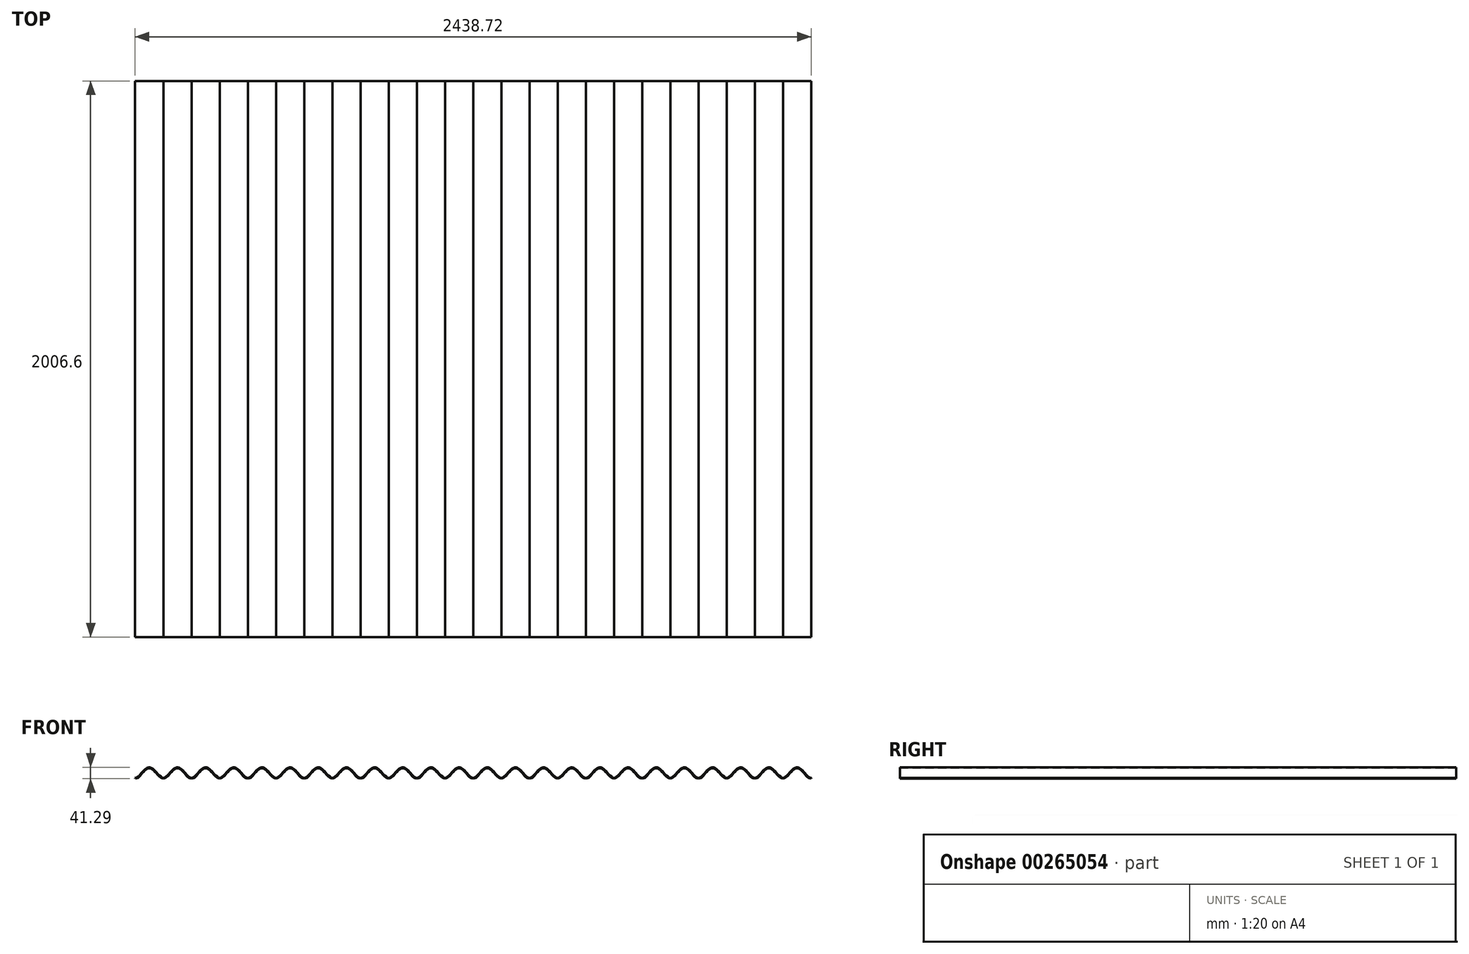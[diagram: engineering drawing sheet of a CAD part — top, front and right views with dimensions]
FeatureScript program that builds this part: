
annotation { "Feature Type Name" : "Feature", "Feature Type Description" : "" }
export const myFeature = defineFeature(function(context is Context, id is Id, definition is map)
    precondition{}
    {
        {
            var Q0;
            Q0=qCreatedBy(makeId("Front.planeOp"),FACE);
            var sketch = newSketch(context, id + "F0", { "sketchPlane" : qUnion([Q0])});
            skFitSpline(sketch, "E0", {"points": [v(-101.6, 0) * mm, v(-76.2, 19.05) * mm, v(-50.8, 38.1) * mm, v(-25.4, 19.05) * mm, v(0, 0) * mm], "startDerivative": vector(131.34, 13.35) * mm, "endDerivative": vector(107.4, -17.1) * mm});
            skLineSegment(sketch, "E1", {"start": v(-101.6, 0) * mm, "end": v(0, 0) * mm, "construction": true});
            skLineSegment(sketch, "E2", {"start": v(-50.8, 49.06) * mm, "end": v(-50.8, -10.5) * mm, "construction": true});
            skPoint(sketch, "E2.endSnap0", {"position": v(-50.8, 0) * mm});
            skFitSpline(sketch, "E3.MirrorCS", {"points": [v(101.6, 0) * mm, v(76.2, 19.05) * mm, v(50.8, 38.1) * mm, v(25.4, 19.05) * mm, v(0, 0) * mm], "startDerivative": vector(-131.34, 13.35) * mm, "endDerivative": vector(-107.4, -17.1) * mm});
            skFitSpline(sketch, "E4.MirrorCS", {"points": [v(101.6, 0) * mm, v(127, 19.05) * mm, v(152.4, 38.1) * mm, v(177.8, 19.05) * mm, v(203.2, 0) * mm], "startDerivative": vector(131.34, 13.35) * mm, "endDerivative": vector(107.4, -17.1) * mm});
            skFitSpline(sketch, "E5.MirrorCS", {"points": [v(304.8, 0) * mm, v(279.4, 19.05) * mm, v(254, 38.1) * mm, v(228.6, 19.05) * mm, v(203.2, 0) * mm], "startDerivative": vector(-131.34, 13.35) * mm, "endDerivative": vector(-107.4, -17.1) * mm});
            skFitSpline(sketch, "E6.MirrorCS", {"points": [v(304.8, 0) * mm, v(330.2, 19.05) * mm, v(355.6, 38.1) * mm, v(381, 19.05) * mm, v(406.4, 0) * mm], "startDerivative": vector(131.34, 13.35) * mm, "endDerivative": vector(107.4, -17.1) * mm});
            skFitSpline(sketch, "E7.MirrorCS", {"points": [v(508, 0) * mm, v(482.6, 19.05) * mm, v(457.2, 38.1) * mm, v(431.8, 19.05) * mm, v(406.4, 0) * mm], "startDerivative": vector(-131.34, 13.35) * mm, "endDerivative": vector(-107.4, -17.1) * mm});
            skFitSpline(sketch, "E8.MirrorCS", {"points": [v(508, 0) * mm, v(533.4, 19.05) * mm, v(558.8, 38.1) * mm, v(584.2, 19.05) * mm, v(609.6, 0) * mm], "startDerivative": vector(131.34, 13.35) * mm, "endDerivative": vector(107.4, -17.1) * mm});
            skFitSpline(sketch, "E9.MirrorCS", {"points": [v(711.2, 0) * mm, v(685.8, 19.05) * mm, v(660.4, 38.1) * mm, v(635, 19.05) * mm, v(609.6, 0) * mm], "startDerivative": vector(-131.34, 13.35) * mm, "endDerivative": vector(-107.4, -17.1) * mm});
            skFitSpline(sketch, "E10.MirrorCS", {"points": [v(711.2, 0) * mm, v(736.6, 19.05) * mm, v(762, 38.1) * mm, v(787.4, 19.05) * mm, v(812.8, 0) * mm], "startDerivative": vector(131.34, 13.35) * mm, "endDerivative": vector(107.4, -17.1) * mm});
            skFitSpline(sketch, "E11.MirrorCS", {"points": [v(914.4, 0) * mm, v(889, 19.05) * mm, v(863.6, 38.1) * mm, v(838.2, 19.05) * mm, v(812.8, 0) * mm], "startDerivative": vector(-131.34, 13.35) * mm, "endDerivative": vector(-107.4, -17.1) * mm});
            skFitSpline(sketch, "E12.MirrorCS", {"points": [v(914.4, 0) * mm, v(939.8, 19.05) * mm, v(965.2, 38.1) * mm, v(990.6, 19.05) * mm, v(1016, 0) * mm], "startDerivative": vector(131.34, 13.35) * mm, "endDerivative": vector(107.4, -17.1) * mm});
            skFitSpline(sketch, "E13.MirrorCS", {"points": [v(1117.6, 0) * mm, v(1092.2, 19.05) * mm, v(1066.8, 38.1) * mm, v(1041.4, 19.05) * mm, v(1016, 0) * mm], "startDerivative": vector(-131.34, 13.35) * mm, "endDerivative": vector(-107.4, -17.1) * mm});
            skFitSpline(sketch, "E14.MirrorCS", {"points": [v(1117.6, 0) * mm, v(1143, 19.05) * mm, v(1168.4, 38.1) * mm, v(1193.8, 19.05) * mm, v(1219.2, 0) * mm], "startDerivative": vector(131.34, 13.35) * mm, "endDerivative": vector(107.4, -17.1) * mm});
            skFitSpline(sketch, "E15.MirrorCS", {"points": [v(1320.8, 0) * mm, v(1295.4, 19.05) * mm, v(1270, 38.1) * mm, v(1244.6, 19.05) * mm, v(1219.2, 0) * mm], "startDerivative": vector(-131.34, 13.35) * mm, "endDerivative": vector(-107.4, -17.1) * mm});
            skFitSpline(sketch, "E16.MirrorCS", {"points": [v(1320.8, 0) * mm, v(1346.2, 19.05) * mm, v(1371.6, 38.1) * mm, v(1397, 19.05) * mm, v(1422.4, 0) * mm], "startDerivative": vector(131.34, 13.35) * mm, "endDerivative": vector(107.4, -17.1) * mm});
            skFitSpline(sketch, "E17.MirrorCS", {"points": [v(1524, 0) * mm, v(1498.6, 19.05) * mm, v(1473.2, 38.1) * mm, v(1447.8, 19.05) * mm, v(1422.4, 0) * mm], "startDerivative": vector(-131.34, 13.35) * mm, "endDerivative": vector(-107.4, -17.1) * mm});
            skFitSpline(sketch, "E18.MirrorCS", {"points": [v(1524, 0) * mm, v(1549.4, 19.05) * mm, v(1574.8, 38.1) * mm, v(1600.2, 19.05) * mm, v(1625.6, 0) * mm], "startDerivative": vector(131.34, 13.35) * mm, "endDerivative": vector(107.4, -17.1) * mm});
            skFitSpline(sketch, "E19.MirrorCS", {"points": [v(1727.2, 0) * mm, v(1701.8, 19.05) * mm, v(1676.4, 38.1) * mm, v(1651, 19.05) * mm, v(1625.6, 0) * mm], "startDerivative": vector(-131.34, 13.35) * mm, "endDerivative": vector(-107.4, -17.1) * mm});
            skFitSpline(sketch, "E20.MirrorCS", {"points": [v(1727.2, 0) * mm, v(1752.6, 19.05) * mm, v(1778, 38.1) * mm, v(1803.4, 19.05) * mm, v(1828.8, 0) * mm], "startDerivative": vector(131.34, 13.35) * mm, "endDerivative": vector(107.4, -17.1) * mm});
            skFitSpline(sketch, "E21.MirrorCS", {"points": [v(1930.4, 0) * mm, v(1905, 19.05) * mm, v(1879.6, 38.1) * mm, v(1854.2, 19.05) * mm, v(1828.8, 0) * mm], "startDerivative": vector(-131.34, 13.35) * mm, "endDerivative": vector(-107.4, -17.1) * mm});
            skFitSpline(sketch, "E22.MirrorCS", {"points": [v(1930.4, 0) * mm, v(1955.8, 19.05) * mm, v(1981.2, 38.1) * mm, v(2006.6, 19.05) * mm, v(2032, 0) * mm], "startDerivative": vector(131.34, 13.35) * mm, "endDerivative": vector(107.4, -17.1) * mm});
            skFitSpline(sketch, "E23.MirrorCS", {"points": [v(2133.6, 0) * mm, v(2108.2, 19.05) * mm, v(2082.8, 38.1) * mm, v(2057.4, 19.05) * mm, v(2032, 0) * mm], "startDerivative": vector(-131.34, 13.35) * mm, "endDerivative": vector(-107.4, -17.1) * mm});
            skFitSpline(sketch, "E24.MirrorCS", {"points": [v(2133.6, 0) * mm, v(2159, 19.05) * mm, v(2184.4, 38.1) * mm, v(2209.8, 19.05) * mm, v(2235.2, 0) * mm], "startDerivative": vector(131.34, 13.35) * mm, "endDerivative": vector(107.4, -17.1) * mm});
            skFitSpline(sketch, "E25.MirrorCS", {"points": [v(2336.8, 0) * mm, v(2311.4, 19.05) * mm, v(2286, 38.1) * mm, v(2260.6, 19.05) * mm, v(2235.2, 0) * mm], "startDerivative": vector(-131.34, 13.35) * mm, "endDerivative": vector(-107.4, -17.1) * mm});
            skFitSpline(sketch, "E26.MirrorCS", {"points": [v(3149.6, 0) * mm, v(3124.2, 19.05) * mm, v(3098.8, 38.1) * mm, v(3073.4, 19.05) * mm, v(3048, 0) * mm], "startDerivative": vector(-131.34, 13.35) * mm, "endDerivative": vector(-107.4, -17.1) * mm});
            skFitSpline(sketch, "E27.MirrorCS", {"points": [v(1930.4, 0) * mm, v(1905, 19.05) * mm, v(1879.6, 38.1) * mm, v(1854.2, 19.05) * mm, v(1828.8, 0) * mm], "startDerivative": vector(-131.34, 13.35) * mm, "endDerivative": vector(-107.4, -17.1) * mm});
            skFitSpline(sketch, "E28.MirrorCS", {"points": [v(1320.8, 0) * mm, v(1295.4, 19.05) * mm, v(1270, 38.1) * mm, v(1244.6, 19.05) * mm, v(1219.2, 0) * mm], "startDerivative": vector(-131.34, 13.35) * mm, "endDerivative": vector(-107.4, -17.1) * mm});
            skFitSpline(sketch, "E29.MirrorCS", {"points": [v(1117.6, 0) * mm, v(1143, 19.05) * mm, v(1168.4, 38.1) * mm, v(1193.8, 19.05) * mm, v(1219.2, 0) * mm], "startDerivative": vector(131.34, 13.35) * mm, "endDerivative": vector(107.4, -17.1) * mm});
            skFitSpline(sketch, "E30.MirrorCS", {"points": [v(1727.2, 0) * mm, v(1752.6, 19.05) * mm, v(1778, 38.1) * mm, v(1803.4, 19.05) * mm, v(1828.8, 0) * mm], "startDerivative": vector(131.34, 13.35) * mm, "endDerivative": vector(107.4, -17.1) * mm});
            skFitSpline(sketch, "E31.MirrorCS", {"points": [v(1930.4, 0) * mm, v(1955.8, 19.05) * mm, v(1981.2, 38.1) * mm, v(2006.6, 19.05) * mm, v(2032, 0) * mm], "startDerivative": vector(131.34, 13.35) * mm, "endDerivative": vector(107.4, -17.1) * mm});
            skFitSpline(sketch, "E32.MirrorCS", {"points": [v(1320.8, 0) * mm, v(1346.2, 19.05) * mm, v(1371.6, 38.1) * mm, v(1397, 19.05) * mm, v(1422.4, 0) * mm], "startDerivative": vector(131.34, 13.35) * mm, "endDerivative": vector(107.4, -17.1) * mm});
            skFitSpline(sketch, "E33.MirrorCS", {"points": [v(1524, 0) * mm, v(1498.6, 19.05) * mm, v(1473.2, 38.1) * mm, v(1447.8, 19.05) * mm, v(1422.4, 0) * mm], "startDerivative": vector(-131.34, 13.35) * mm, "endDerivative": vector(-107.4, -17.1) * mm});
            skFitSpline(sketch, "E34.MirrorCS", {"points": [v(2336.8, 0) * mm, v(2311.4, 19.05) * mm, v(2286, 38.1) * mm, v(2260.6, 19.05) * mm, v(2235.2, 0) * mm], "startDerivative": vector(-131.34, 13.35) * mm, "endDerivative": vector(-107.4, -17.1) * mm});
            skFitSpline(sketch, "E35.MirrorCS", {"points": [v(2336.8, 0) * mm, v(2362.2, 19.05) * mm, v(2387.6, 38.1) * mm, v(2413, 19.05) * mm, v(2438.4, 0) * mm], "startDerivative": vector(131.34, 13.35) * mm, "endDerivative": vector(107.4, -17.1) * mm});
            skFitSpline(sketch, "E36.MirrorCS", {"points": [v(2540, 0) * mm, v(2514.6, 19.05) * mm, v(2489.2, 38.1) * mm, v(2463.8, 19.05) * mm, v(2438.4, 0) * mm], "startDerivative": vector(-131.34, 13.35) * mm, "endDerivative": vector(-107.4, -17.1) * mm});
            skFitSpline(sketch, "E37.MirrorCS", {"points": [v(2540, 0) * mm, v(2565.4, 19.05) * mm, v(2590.8, 38.1) * mm, v(2616.2, 19.05) * mm, v(2641.6, 0) * mm], "startDerivative": vector(131.34, 13.35) * mm, "endDerivative": vector(107.4, -17.1) * mm});
            skFitSpline(sketch, "E38.MirrorCS", {"points": [v(2743.2, 0) * mm, v(2717.8, 19.05) * mm, v(2692.4, 38.1) * mm, v(2667, 19.05) * mm, v(2641.6, 0) * mm], "startDerivative": vector(-131.34, 13.35) * mm, "endDerivative": vector(-107.4, -17.1) * mm});
            skFitSpline(sketch, "E39.MirrorCS", {"points": [v(2133.6, 0) * mm, v(2159, 19.05) * mm, v(2184.4, 38.1) * mm, v(2209.8, 19.05) * mm, v(2235.2, 0) * mm], "startDerivative": vector(131.34, 13.35) * mm, "endDerivative": vector(107.4, -17.1) * mm});
            skFitSpline(sketch, "E40.MirrorCS", {"points": [v(1727.2, 0) * mm, v(1701.8, 19.05) * mm, v(1676.4, 38.1) * mm, v(1651, 19.05) * mm, v(1625.6, 0) * mm], "startDerivative": vector(-131.34, 13.35) * mm, "endDerivative": vector(-107.4, -17.1) * mm});
            skFitSpline(sketch, "E41.MirrorCS", {"points": [v(2743.2, 0) * mm, v(2768.6, 19.05) * mm, v(2794, 38.1) * mm, v(2819.4, 19.05) * mm, v(2844.8, 0) * mm], "startDerivative": vector(131.34, 13.35) * mm, "endDerivative": vector(107.4, -17.1) * mm});
            skFitSpline(sketch, "E42.MirrorCS", {"points": [v(1524, 0) * mm, v(1549.4, 19.05) * mm, v(1574.8, 38.1) * mm, v(1600.2, 19.05) * mm, v(1625.6, 0) * mm], "startDerivative": vector(131.34, 13.35) * mm, "endDerivative": vector(107.4, -17.1) * mm});
            skFitSpline(sketch, "E43.MirrorCS", {"points": [v(914.4, 0) * mm, v(939.8, 19.05) * mm, v(965.2, 38.1) * mm, v(990.6, 19.05) * mm, v(1016, 0) * mm], "startDerivative": vector(131.34, 13.35) * mm, "endDerivative": vector(107.4, -17.1) * mm});
            skFitSpline(sketch, "E44.MirrorCS", {"points": [v(2946.4, 0) * mm, v(2921, 19.05) * mm, v(2895.6, 38.1) * mm, v(2870.2, 19.05) * mm, v(2844.8, 0) * mm], "startDerivative": vector(-131.34, 13.35) * mm, "endDerivative": vector(-107.4, -17.1) * mm});
            skFitSpline(sketch, "E45.MirrorCS", {"points": [v(1117.6, 0) * mm, v(1092.2, 19.05) * mm, v(1066.8, 38.1) * mm, v(1041.4, 19.05) * mm, v(1016, 0) * mm], "startDerivative": vector(-131.34, 13.35) * mm, "endDerivative": vector(-107.4, -17.1) * mm});
            skFitSpline(sketch, "E46.MirrorCS", {"points": [v(711.2, 0) * mm, v(736.6, 19.05) * mm, v(762, 38.1) * mm, v(787.4, 19.05) * mm, v(812.8, 0) * mm], "startDerivative": vector(131.34, 13.35) * mm, "endDerivative": vector(107.4, -17.1) * mm});
            skFitSpline(sketch, "E47.MirrorCS", {"points": [v(2946.4, 0) * mm, v(2971.8, 19.05) * mm, v(2997.2, 38.1) * mm, v(3022.6, 19.05) * mm, v(3048, 0) * mm], "startDerivative": vector(131.34, 13.35) * mm, "endDerivative": vector(107.4, -17.1) * mm});
            skFitSpline(sketch, "E48.MirrorCS", {"points": [v(914.4, 0) * mm, v(889, 19.05) * mm, v(863.6, 38.1) * mm, v(838.2, 19.05) * mm, v(812.8, 0) * mm], "startDerivative": vector(-131.34, 13.35) * mm, "endDerivative": vector(-107.4, -17.1) * mm});
            skFitSpline(sketch, "E49.MirrorCS", {"points": [v(914.4, 0) * mm, v(889, 19.05) * mm, v(863.6, 38.1) * mm, v(838.2, 19.05) * mm, v(812.8, 0) * mm], "startDerivative": vector(-131.34, 13.35) * mm, "endDerivative": vector(-107.4, -17.1) * mm});
            skFitSpline(sketch, "E50.MirrorCS", {"points": [v(2133.6, 0) * mm, v(2159, 19.05) * mm, v(2184.4, 38.1) * mm, v(2209.8, 19.05) * mm, v(2235.2, 0) * mm], "startDerivative": vector(131.34, 13.35) * mm, "endDerivative": vector(107.4, -17.1) * mm});
            skFitSpline(sketch, "E51.MirrorCS", {"points": [v(914.4, 0) * mm, v(939.8, 19.05) * mm, v(965.2, 38.1) * mm, v(990.6, 19.05) * mm, v(1016, 0) * mm], "startDerivative": vector(131.34, 13.35) * mm, "endDerivative": vector(107.4, -17.1) * mm});
            skFitSpline(sketch, "E52.MirrorCS", {"points": [v(1524, 0) * mm, v(1498.6, 19.05) * mm, v(1473.2, 38.1) * mm, v(1447.8, 19.05) * mm, v(1422.4, 0) * mm], "startDerivative": vector(-131.34, 13.35) * mm, "endDerivative": vector(-107.4, -17.1) * mm});
            skFitSpline(sketch, "E53.MirrorCS", {"points": [v(1320.8, 0) * mm, v(1346.2, 19.05) * mm, v(1371.6, 38.1) * mm, v(1397, 19.05) * mm, v(1422.4, 0) * mm], "startDerivative": vector(131.34, 13.35) * mm, "endDerivative": vector(107.4, -17.1) * mm});
            skFitSpline(sketch, "E54.MirrorCS", {"points": [v(1524, 0) * mm, v(1549.4, 19.05) * mm, v(1574.8, 38.1) * mm, v(1600.2, 19.05) * mm, v(1625.6, 0) * mm], "startDerivative": vector(131.34, 13.35) * mm, "endDerivative": vector(107.4, -17.1) * mm});
            skFitSpline(sketch, "E55.MirrorCS", {"points": [v(1727.2, 0) * mm, v(1752.6, 19.05) * mm, v(1778, 38.1) * mm, v(1803.4, 19.05) * mm, v(1828.8, 0) * mm], "startDerivative": vector(131.34, 13.35) * mm, "endDerivative": vector(107.4, -17.1) * mm});
            skFitSpline(sketch, "E56.MirrorCS", {"points": [v(2133.6, 0) * mm, v(2108.2, 19.05) * mm, v(2082.8, 38.1) * mm, v(2057.4, 19.05) * mm, v(2032, 0) * mm], "startDerivative": vector(-131.34, 13.35) * mm, "endDerivative": vector(-107.4, -17.1) * mm});
            skFitSpline(sketch, "E57.MirrorCS", {"points": [v(1320.8, 0) * mm, v(1295.4, 19.05) * mm, v(1270, 38.1) * mm, v(1244.6, 19.05) * mm, v(1219.2, 0) * mm], "startDerivative": vector(-131.34, 13.35) * mm, "endDerivative": vector(-107.4, -17.1) * mm});
            skFitSpline(sketch, "E58.MirrorCS", {"points": [v(711.2, 0) * mm, v(736.6, 19.05) * mm, v(762, 38.1) * mm, v(787.4, 19.05) * mm, v(812.8, 0) * mm], "startDerivative": vector(131.34, 13.35) * mm, "endDerivative": vector(107.4, -17.1) * mm});
            skFitSpline(sketch, "E59.MirrorCS", {"points": [v(2336.8, 0) * mm, v(2311.4, 19.05) * mm, v(2286, 38.1) * mm, v(2260.6, 19.05) * mm, v(2235.2, 0) * mm], "startDerivative": vector(-131.34, 13.35) * mm, "endDerivative": vector(-107.4, -17.1) * mm});
            skFitSpline(sketch, "E60.MirrorCS", {"points": [v(1117.6, 0) * mm, v(1143, 19.05) * mm, v(1168.4, 38.1) * mm, v(1193.8, 19.05) * mm, v(1219.2, 0) * mm], "startDerivative": vector(131.34, 13.35) * mm, "endDerivative": vector(107.4, -17.1) * mm});
            skFitSpline(sketch, "E61.MirrorCS", {"points": [v(1930.4, 0) * mm, v(1955.8, 19.05) * mm, v(1981.2, 38.1) * mm, v(2006.6, 19.05) * mm, v(2032, 0) * mm], "startDerivative": vector(131.34, 13.35) * mm, "endDerivative": vector(107.4, -17.1) * mm});
            skFitSpline(sketch, "E62.MirrorCS", {"points": [v(1930.4, 0) * mm, v(1905, 19.05) * mm, v(1879.6, 38.1) * mm, v(1854.2, 19.05) * mm, v(1828.8, 0) * mm], "startDerivative": vector(-131.34, 13.35) * mm, "endDerivative": vector(-107.4, -17.1) * mm});
            skFitSpline(sketch, "E63.MirrorCS", {"points": [v(1117.6, 0) * mm, v(1092.2, 19.05) * mm, v(1066.8, 38.1) * mm, v(1041.4, 19.05) * mm, v(1016, 0) * mm], "startDerivative": vector(-131.34, 13.35) * mm, "endDerivative": vector(-107.4, -17.1) * mm});
            skFitSpline(sketch, "E64.MirrorCS", {"points": [v(1727.2, 0) * mm, v(1701.8, 19.05) * mm, v(1676.4, 38.1) * mm, v(1651, 19.05) * mm, v(1625.6, 0) * mm], "startDerivative": vector(-131.34, 13.35) * mm, "endDerivative": vector(-107.4, -17.1) * mm});
            skFitSpline(sketch, "E65.MirrorCS", {"points": [v(1524, 0) * mm, v(1498.6, 19.05) * mm, v(1473.2, 38.1) * mm, v(1447.8, 19.05) * mm, v(1422.4, 0) * mm], "startDerivative": vector(-131.34, 13.35) * mm, "endDerivative": vector(-107.4, -17.1) * mm});
            skFitSpline(sketch, "E66.MirrorCS", {"points": [v(1930.4, 0) * mm, v(1955.8, 19.05) * mm, v(1981.2, 38.1) * mm, v(2006.6, 19.05) * mm, v(2032, 0) * mm], "startDerivative": vector(131.34, 13.35) * mm, "endDerivative": vector(107.4, -17.1) * mm});
            skFitSpline(sketch, "E67.MirrorCS", {"points": [v(1320.8, 0) * mm, v(1346.2, 19.05) * mm, v(1371.6, 38.1) * mm, v(1397, 19.05) * mm, v(1422.4, 0) * mm], "startDerivative": vector(131.34, 13.35) * mm, "endDerivative": vector(107.4, -17.1) * mm});
            skFitSpline(sketch, "E68.MirrorCS", {"points": [v(2133.6, 0) * mm, v(2108.2, 19.05) * mm, v(2082.8, 38.1) * mm, v(2057.4, 19.05) * mm, v(2032, 0) * mm], "startDerivative": vector(-131.34, 13.35) * mm, "endDerivative": vector(-107.4, -17.1) * mm});
            skFitSpline(sketch, "E69.MirrorCS", {"points": [v(3149.6, 0) * mm, v(3124.2, 19.05) * mm, v(3098.8, 38.1) * mm, v(3073.4, 19.05) * mm, v(3048, 0) * mm], "startDerivative": vector(-131.34, 13.35) * mm, "endDerivative": vector(-107.4, -17.1) * mm});
            skFitSpline(sketch, "E70.MirrorCS", {"points": [v(2133.6, 0) * mm, v(2159, 19.05) * mm, v(2184.4, 38.1) * mm, v(2209.8, 19.05) * mm, v(2235.2, 0) * mm], "startDerivative": vector(131.34, 13.35) * mm, "endDerivative": vector(107.4, -17.1) * mm});
            skFitSpline(sketch, "E71.MirrorCS", {"points": [v(2336.8, 0) * mm, v(2311.4, 19.05) * mm, v(2286, 38.1) * mm, v(2260.6, 19.05) * mm, v(2235.2, 0) * mm], "startDerivative": vector(-131.34, 13.35) * mm, "endDerivative": vector(-107.4, -17.1) * mm});
            skFitSpline(sketch, "E72.MirrorCS", {"points": [v(1117.6, 0) * mm, v(1092.2, 19.05) * mm, v(1066.8, 38.1) * mm, v(1041.4, 19.05) * mm, v(1016, 0) * mm], "startDerivative": vector(-131.34, 13.35) * mm, "endDerivative": vector(-107.4, -17.1) * mm});
            skFitSpline(sketch, "E73.MirrorCS", {"points": [v(1727.2, 0) * mm, v(1701.8, 19.05) * mm, v(1676.4, 38.1) * mm, v(1651, 19.05) * mm, v(1625.6, 0) * mm], "startDerivative": vector(-131.34, 13.35) * mm, "endDerivative": vector(-107.4, -17.1) * mm});
            skFitSpline(sketch, "E74.MirrorCS", {"points": [v(1320.8, 0) * mm, v(1295.4, 19.05) * mm, v(1270, 38.1) * mm, v(1244.6, 19.05) * mm, v(1219.2, 0) * mm], "startDerivative": vector(-131.34, 13.35) * mm, "endDerivative": vector(-107.4, -17.1) * mm});
            skFitSpline(sketch, "E75.MirrorCS", {"points": [v(1727.2, 0) * mm, v(1752.6, 19.05) * mm, v(1778, 38.1) * mm, v(1803.4, 19.05) * mm, v(1828.8, 0) * mm], "startDerivative": vector(131.34, 13.35) * mm, "endDerivative": vector(107.4, -17.1) * mm});
            skFitSpline(sketch, "E76.MirrorCS", {"points": [v(304.8, 0) * mm, v(279.4, 19.05) * mm, v(254, 38.1) * mm, v(228.6, 19.05) * mm, v(203.2, 0) * mm], "startDerivative": vector(-131.34, 13.35) * mm, "endDerivative": vector(-107.4, -17.1) * mm});
            skFitSpline(sketch, "E77.MirrorCS", {"points": [v(2336.8, 0) * mm, v(2362.2, 19.05) * mm, v(2387.6, 38.1) * mm, v(2413, 19.05) * mm, v(2438.4, 0) * mm], "startDerivative": vector(131.34, 13.35) * mm, "endDerivative": vector(107.4, -17.1) * mm});
            skFitSpline(sketch, "E78.MirrorCS", {"points": [v(2540, 0) * mm, v(2514.6, 19.05) * mm, v(2489.2, 38.1) * mm, v(2463.8, 19.05) * mm, v(2438.4, 0) * mm], "startDerivative": vector(-131.34, 13.35) * mm, "endDerivative": vector(-107.4, -17.1) * mm});
            skFitSpline(sketch, "E79.MirrorCS", {"points": [v(2540, 0) * mm, v(2565.4, 19.05) * mm, v(2590.8, 38.1) * mm, v(2616.2, 19.05) * mm, v(2641.6, 0) * mm], "startDerivative": vector(131.34, 13.35) * mm, "endDerivative": vector(107.4, -17.1) * mm});
            skFitSpline(sketch, "E80.MirrorCS", {"points": [v(2743.2, 0) * mm, v(2717.8, 19.05) * mm, v(2692.4, 38.1) * mm, v(2667, 19.05) * mm, v(2641.6, 0) * mm], "startDerivative": vector(-131.34, 13.35) * mm, "endDerivative": vector(-107.4, -17.1) * mm});
            skFitSpline(sketch, "E81.MirrorCS", {"points": [v(2743.2, 0) * mm, v(2768.6, 19.05) * mm, v(2794, 38.1) * mm, v(2819.4, 19.05) * mm, v(2844.8, 0) * mm], "startDerivative": vector(131.34, 13.35) * mm, "endDerivative": vector(107.4, -17.1) * mm});
            skFitSpline(sketch, "E82.MirrorCS", {"points": [v(2946.4, 0) * mm, v(2921, 19.05) * mm, v(2895.6, 38.1) * mm, v(2870.2, 19.05) * mm, v(2844.8, 0) * mm], "startDerivative": vector(-131.34, 13.35) * mm, "endDerivative": vector(-107.4, -17.1) * mm});
            skFitSpline(sketch, "E83.MirrorCS", {"points": [v(2946.4, 0) * mm, v(2971.8, 19.05) * mm, v(2997.2, 38.1) * mm, v(3022.6, 19.05) * mm, v(3048, 0) * mm], "startDerivative": vector(131.34, 13.35) * mm, "endDerivative": vector(107.4, -17.1) * mm});
            skFitSpline(sketch, "E84.MirrorCS", {"points": [v(304.8, 0) * mm, v(330.2, 19.05) * mm, v(355.6, 38.1) * mm, v(381, 19.05) * mm, v(406.4, 0) * mm], "startDerivative": vector(131.34, 13.35) * mm, "endDerivative": vector(107.4, -17.1) * mm});
            skFitSpline(sketch, "E85.MirrorCS", {"points": [v(508, 0) * mm, v(533.4, 19.05) * mm, v(558.8, 38.1) * mm, v(584.2, 19.05) * mm, v(609.6, 0) * mm], "startDerivative": vector(131.34, 13.35) * mm, "endDerivative": vector(107.4, -17.1) * mm});
            skFitSpline(sketch, "E86.MirrorCS", {"points": [v(711.2, 0) * mm, v(685.8, 19.05) * mm, v(660.4, 38.1) * mm, v(635, 19.05) * mm, v(609.6, 0) * mm], "startDerivative": vector(-131.34, 13.35) * mm, "endDerivative": vector(-107.4, -17.1) * mm});
            skFitSpline(sketch, "E87.0", {"points": [v(-101.92, 3.16) * mm, v(-100.74, 3.28) * mm, v(-98.53, 3.72) * mm, v(-95.48, 4.91) * mm, v(-92.58, 6.62) * mm, v(-89.79, 8.8) * mm, v(-87.04, 11.42) * mm, v(-84.3, 14.39) * mm, v(-81.52, 17.64) * mm, v(-78.65, 21.08) * mm, v(-75.64, 24.62) * mm, v(-72.5, 28.12) * mm, v(-69.26, 31.47) * mm, v(-65.9, 34.55) * mm, v(-62.4, 37.23) * mm, v(-59.37, 39.04) * mm, v(-56.83, 40.15) * mm, v(-54.87, 40.78) * mm, v(-53.2, 41.11) * mm, v(-51.83, 41.25) * mm, v(-50.8, 41.29) * mm, v(-49.76, 41.25) * mm, v(-48.4, 41.1) * mm, v(-46.72, 40.75) * mm, v(-44.78, 40.11) * mm, v(-42.28, 38.99) * mm, v(-39.3, 37.17) * mm, v(-35.87, 34.48) * mm, v(-32.56, 31.41) * mm, v(-29.33, 28.1) * mm, v(-26.16, 24.63) * mm, v(-23.04, 21.16) * mm, v(-19.97, 17.8) * mm, v(-15.9, 13.53) * mm, v(-11.9, 9.76) * mm, v(-7.98, 6.78) * mm, v(-5.08, 5.01) * mm, v(-2.25, 3.76) * mm, v(-0.42, 3.28) * mm, v(0.5, 3.14) * mm]});
            skFitSpline(sketch, "E87.1", {"points": [v(101.92, 3.16) * mm, v(100.74, 3.28) * mm, v(98.53, 3.72) * mm, v(95.48, 4.91) * mm, v(92.58, 6.62) * mm, v(89.79, 8.8) * mm, v(87.04, 11.42) * mm, v(84.3, 14.39) * mm, v(81.52, 17.64) * mm, v(78.65, 21.08) * mm, v(75.64, 24.62) * mm, v(72.5, 28.12) * mm, v(69.26, 31.47) * mm, v(65.9, 34.55) * mm, v(62.4, 37.23) * mm, v(59.37, 39.04) * mm, v(56.83, 40.15) * mm, v(54.87, 40.78) * mm, v(53.2, 41.11) * mm, v(51.83, 41.25) * mm, v(50.8, 41.29) * mm, v(49.76, 41.25) * mm, v(48.4, 41.1) * mm, v(46.72, 40.75) * mm, v(44.78, 40.11) * mm, v(42.28, 38.99) * mm, v(39.3, 37.17) * mm, v(35.87, 34.48) * mm, v(32.56, 31.41) * mm, v(29.33, 28.1) * mm, v(26.16, 24.63) * mm, v(23.04, 21.16) * mm, v(19.97, 17.8) * mm, v(15.9, 13.53) * mm, v(11.9, 9.76) * mm, v(7.98, 6.78) * mm, v(5.08, 5.01) * mm, v(2.25, 3.76) * mm, v(0.42, 3.28) * mm, v(-0.5, 3.14) * mm]});
            skFitSpline(sketch, "E87.2", {"points": [v(101.28, 3.16) * mm, v(102.46, 3.28) * mm, v(104.67, 3.72) * mm, v(107.72, 4.91) * mm, v(110.62, 6.62) * mm, v(113.41, 8.8) * mm, v(116.16, 11.42) * mm, v(118.9, 14.39) * mm, v(121.68, 17.64) * mm, v(124.55, 21.08) * mm, v(127.56, 24.62) * mm, v(130.7, 28.12) * mm, v(133.94, 31.47) * mm, v(137.3, 34.55) * mm, v(140.8, 37.23) * mm, v(143.83, 39.04) * mm, v(146.37, 40.15) * mm, v(148.33, 40.78) * mm, v(150, 41.11) * mm, v(151.37, 41.25) * mm, v(152.4, 41.29) * mm, v(153.44, 41.25) * mm, v(154.8, 41.1) * mm, v(156.48, 40.75) * mm, v(158.42, 40.11) * mm, v(160.92, 38.99) * mm, v(163.9, 37.17) * mm, v(167.33, 34.48) * mm, v(170.64, 31.41) * mm, v(173.87, 28.1) * mm, v(177.04, 24.63) * mm, v(180.16, 21.16) * mm, v(183.23, 17.8) * mm, v(187.3, 13.53) * mm, v(191.3, 9.76) * mm, v(195.22, 6.78) * mm, v(198.12, 5.01) * mm, v(200.95, 3.76) * mm, v(202.78, 3.28) * mm, v(203.7, 3.14) * mm]});
            skFitSpline(sketch, "E87.3", {"points": [v(305.12, 3.16) * mm, v(303.94, 3.28) * mm, v(301.73, 3.72) * mm, v(298.68, 4.91) * mm, v(295.78, 6.62) * mm, v(292.99, 8.8) * mm, v(290.24, 11.42) * mm, v(287.5, 14.39) * mm, v(284.72, 17.64) * mm, v(281.85, 21.08) * mm, v(278.84, 24.62) * mm, v(275.7, 28.12) * mm, v(272.46, 31.47) * mm, v(269.1, 34.55) * mm, v(265.6, 37.23) * mm, v(262.57, 39.04) * mm, v(260.03, 40.15) * mm, v(258.07, 40.78) * mm, v(256.4, 41.11) * mm, v(255.03, 41.25) * mm, v(254, 41.29) * mm, v(252.96, 41.25) * mm, v(251.6, 41.1) * mm, v(249.92, 40.75) * mm, v(247.98, 40.11) * mm, v(245.48, 38.99) * mm, v(242.5, 37.17) * mm, v(239.07, 34.48) * mm, v(235.76, 31.41) * mm, v(232.53, 28.1) * mm, v(229.36, 24.63) * mm, v(226.24, 21.16) * mm, v(223.17, 17.8) * mm, v(219.1, 13.53) * mm, v(215.1, 9.76) * mm, v(211.18, 6.78) * mm, v(208.28, 5.01) * mm, v(205.45, 3.76) * mm, v(203.62, 3.28) * mm, v(202.7, 3.14) * mm]});
            skFitSpline(sketch, "E87.4", {"points": [v(304.48, 3.16) * mm, v(305.66, 3.28) * mm, v(307.87, 3.72) * mm, v(310.92, 4.91) * mm, v(313.82, 6.62) * mm, v(316.61, 8.8) * mm, v(319.36, 11.42) * mm, v(322.1, 14.39) * mm, v(324.88, 17.64) * mm, v(327.75, 21.08) * mm, v(330.76, 24.62) * mm, v(333.9, 28.12) * mm, v(337.14, 31.47) * mm, v(340.5, 34.55) * mm, v(344, 37.23) * mm, v(347.03, 39.04) * mm, v(349.57, 40.15) * mm, v(351.53, 40.78) * mm, v(353.2, 41.11) * mm, v(354.57, 41.25) * mm, v(355.6, 41.29) * mm, v(356.64, 41.25) * mm, v(358, 41.1) * mm, v(359.68, 40.75) * mm, v(361.62, 40.11) * mm, v(364.12, 38.99) * mm, v(367.1, 37.17) * mm, v(370.53, 34.48) * mm, v(373.84, 31.41) * mm, v(377.07, 28.1) * mm, v(380.24, 24.63) * mm, v(383.36, 21.16) * mm, v(386.43, 17.8) * mm, v(390.5, 13.53) * mm, v(394.5, 9.76) * mm, v(398.42, 6.78) * mm, v(401.32, 5.01) * mm, v(404.15, 3.76) * mm, v(405.98, 3.28) * mm, v(406.9, 3.14) * mm]});
            skFitSpline(sketch, "E87.5", {"points": [v(508.32, 3.16) * mm, v(507.14, 3.28) * mm, v(504.93, 3.72) * mm, v(501.88, 4.91) * mm, v(498.98, 6.62) * mm, v(496.19, 8.8) * mm, v(493.44, 11.42) * mm, v(490.7, 14.39) * mm, v(487.92, 17.64) * mm, v(485.05, 21.08) * mm, v(482.04, 24.62) * mm, v(478.9, 28.12) * mm, v(475.66, 31.47) * mm, v(472.3, 34.55) * mm, v(468.8, 37.23) * mm, v(465.77, 39.04) * mm, v(463.23, 40.15) * mm, v(461.27, 40.78) * mm, v(459.6, 41.11) * mm, v(458.23, 41.25) * mm, v(457.2, 41.29) * mm, v(456.16, 41.25) * mm, v(454.8, 41.1) * mm, v(453.12, 40.75) * mm, v(451.18, 40.11) * mm, v(448.68, 38.99) * mm, v(445.7, 37.17) * mm, v(442.27, 34.48) * mm, v(438.96, 31.41) * mm, v(435.73, 28.1) * mm, v(432.56, 24.63) * mm, v(429.44, 21.16) * mm, v(426.37, 17.8) * mm, v(422.3, 13.53) * mm, v(418.3, 9.76) * mm, v(414.38, 6.78) * mm, v(411.48, 5.01) * mm, v(408.65, 3.76) * mm, v(406.82, 3.28) * mm, v(405.9, 3.14) * mm]});
            skFitSpline(sketch, "E87.6", {"points": [v(507.68, 3.16) * mm, v(508.86, 3.28) * mm, v(511.07, 3.72) * mm, v(514.12, 4.91) * mm, v(517.02, 6.62) * mm, v(519.81, 8.8) * mm, v(522.56, 11.42) * mm, v(525.3, 14.39) * mm, v(528.08, 17.64) * mm, v(530.95, 21.08) * mm, v(533.96, 24.62) * mm, v(537.1, 28.12) * mm, v(540.34, 31.47) * mm, v(543.7, 34.55) * mm, v(547.2, 37.23) * mm, v(550.23, 39.04) * mm, v(552.77, 40.15) * mm, v(554.73, 40.78) * mm, v(556.4, 41.11) * mm, v(557.77, 41.25) * mm, v(558.8, 41.29) * mm, v(559.84, 41.25) * mm, v(561.2, 41.1) * mm, v(562.88, 40.75) * mm, v(564.82, 40.11) * mm, v(567.32, 38.99) * mm, v(570.3, 37.17) * mm, v(573.73, 34.48) * mm, v(577.04, 31.41) * mm, v(580.27, 28.1) * mm, v(583.44, 24.63) * mm, v(586.56, 21.16) * mm, v(589.63, 17.8) * mm, v(593.7, 13.53) * mm, v(597.7, 9.76) * mm, v(601.62, 6.78) * mm, v(604.52, 5.01) * mm, v(607.35, 3.76) * mm, v(609.18, 3.28) * mm, v(610.1, 3.14) * mm]});
            skFitSpline(sketch, "E87.7", {"points": [v(711.52, 3.16) * mm, v(710.34, 3.28) * mm, v(708.13, 3.72) * mm, v(705.08, 4.91) * mm, v(702.18, 6.62) * mm, v(699.39, 8.8) * mm, v(696.64, 11.42) * mm, v(693.9, 14.39) * mm, v(691.12, 17.64) * mm, v(688.25, 21.08) * mm, v(685.24, 24.62) * mm, v(682.1, 28.12) * mm, v(678.86, 31.47) * mm, v(675.5, 34.55) * mm, v(672, 37.23) * mm, v(668.97, 39.04) * mm, v(666.43, 40.15) * mm, v(664.47, 40.78) * mm, v(662.8, 41.11) * mm, v(661.43, 41.25) * mm, v(660.4, 41.29) * mm, v(659.36, 41.25) * mm, v(658, 41.1) * mm, v(656.32, 40.75) * mm, v(654.38, 40.11) * mm, v(651.88, 38.99) * mm, v(648.9, 37.17) * mm, v(645.47, 34.48) * mm, v(642.16, 31.41) * mm, v(638.93, 28.1) * mm, v(635.76, 24.63) * mm, v(632.64, 21.16) * mm, v(629.57, 17.8) * mm, v(625.5, 13.53) * mm, v(621.5, 9.76) * mm, v(617.58, 6.78) * mm, v(614.68, 5.01) * mm, v(611.85, 3.76) * mm, v(610.02, 3.28) * mm, v(609.1, 3.14) * mm]});
            skFitSpline(sketch, "E87.8", {"points": [v(710.88, 3.16) * mm, v(712.06, 3.28) * mm, v(714.27, 3.72) * mm, v(717.32, 4.91) * mm, v(720.22, 6.62) * mm, v(723.01, 8.8) * mm, v(725.76, 11.42) * mm, v(728.5, 14.39) * mm, v(731.28, 17.64) * mm, v(734.15, 21.08) * mm, v(737.16, 24.62) * mm, v(740.3, 28.12) * mm, v(743.54, 31.47) * mm, v(746.9, 34.55) * mm, v(750.4, 37.23) * mm, v(753.43, 39.04) * mm, v(755.97, 40.15) * mm, v(757.93, 40.78) * mm, v(759.6, 41.11) * mm, v(760.97, 41.25) * mm, v(762, 41.29) * mm, v(763.04, 41.25) * mm, v(764.4, 41.1) * mm, v(766.08, 40.75) * mm, v(768.02, 40.11) * mm, v(770.52, 38.99) * mm, v(773.5, 37.17) * mm, v(776.93, 34.48) * mm, v(780.24, 31.41) * mm, v(783.47, 28.1) * mm, v(786.64, 24.63) * mm, v(789.76, 21.16) * mm, v(792.83, 17.8) * mm, v(796.9, 13.53) * mm, v(800.9, 9.76) * mm, v(804.82, 6.78) * mm, v(807.72, 5.01) * mm, v(810.55, 3.76) * mm, v(812.38, 3.28) * mm, v(813.3, 3.14) * mm]});
            skFitSpline(sketch, "E87.9", {"points": [v(914.72, 3.16) * mm, v(913.54, 3.28) * mm, v(911.33, 3.72) * mm, v(908.28, 4.91) * mm, v(905.38, 6.62) * mm, v(902.59, 8.8) * mm, v(899.84, 11.42) * mm, v(897.1, 14.39) * mm, v(894.32, 17.64) * mm, v(891.45, 21.08) * mm, v(888.44, 24.62) * mm, v(885.3, 28.12) * mm, v(882.06, 31.47) * mm, v(878.7, 34.55) * mm, v(875.2, 37.23) * mm, v(872.17, 39.04) * mm, v(869.63, 40.15) * mm, v(867.67, 40.78) * mm, v(866, 41.11) * mm, v(864.63, 41.25) * mm, v(863.6, 41.29) * mm, v(862.56, 41.25) * mm, v(861.2, 41.1) * mm, v(859.52, 40.75) * mm, v(857.58, 40.11) * mm, v(855.08, 38.99) * mm, v(852.1, 37.17) * mm, v(848.67, 34.48) * mm, v(845.36, 31.41) * mm, v(842.13, 28.1) * mm, v(838.96, 24.63) * mm, v(835.84, 21.16) * mm, v(832.77, 17.8) * mm, v(828.7, 13.53) * mm, v(824.7, 9.76) * mm, v(820.78, 6.78) * mm, v(817.88, 5.01) * mm, v(815.05, 3.76) * mm, v(813.22, 3.28) * mm, v(812.3, 3.14) * mm]});
            skFitSpline(sketch, "E87.10", {"points": [v(2133.28, 3.16) * mm, v(2134.46, 3.28) * mm, v(2136.67, 3.72) * mm, v(2139.72, 4.91) * mm, v(2142.62, 6.62) * mm, v(2145.41, 8.8) * mm, v(2148.16, 11.42) * mm, v(2150.9, 14.39) * mm, v(2153.68, 17.64) * mm, v(2156.55, 21.08) * mm, v(2159.56, 24.62) * mm, v(2162.7, 28.12) * mm, v(2165.94, 31.47) * mm, v(2169.3, 34.55) * mm, v(2172.8, 37.23) * mm, v(2175.83, 39.04) * mm, v(2178.37, 40.15) * mm, v(2180.33, 40.78) * mm, v(2182, 41.11) * mm, v(2183.37, 41.25) * mm, v(2184.4, 41.29) * mm, v(2185.44, 41.25) * mm, v(2186.8, 41.1) * mm, v(2188.48, 40.75) * mm, v(2190.42, 40.11) * mm, v(2192.92, 38.99) * mm, v(2195.9, 37.17) * mm, v(2199.33, 34.48) * mm, v(2202.64, 31.41) * mm, v(2205.87, 28.1) * mm, v(2209.04, 24.63) * mm, v(2212.16, 21.16) * mm, v(2215.23, 17.8) * mm, v(2219.3, 13.53) * mm, v(2223.3, 9.76) * mm, v(2227.22, 6.78) * mm, v(2230.12, 5.01) * mm, v(2232.95, 3.76) * mm, v(2234.78, 3.28) * mm, v(2235.7, 3.14) * mm]});
            skFitSpline(sketch, "E87.11", {"points": [v(2337.12, 3.16) * mm, v(2335.94, 3.28) * mm, v(2333.73, 3.72) * mm, v(2330.68, 4.91) * mm, v(2327.78, 6.62) * mm, v(2324.99, 8.8) * mm, v(2322.24, 11.42) * mm, v(2319.5, 14.39) * mm, v(2316.72, 17.64) * mm, v(2313.85, 21.08) * mm, v(2310.84, 24.62) * mm, v(2307.7, 28.12) * mm, v(2304.46, 31.47) * mm, v(2301.1, 34.55) * mm, v(2297.6, 37.23) * mm, v(2294.57, 39.04) * mm, v(2292.03, 40.15) * mm, v(2290.07, 40.78) * mm, v(2288.4, 41.11) * mm, v(2287.03, 41.25) * mm, v(2286, 41.29) * mm, v(2284.96, 41.25) * mm, v(2283.6, 41.1) * mm, v(2281.92, 40.75) * mm, v(2279.98, 40.11) * mm, v(2277.48, 38.99) * mm, v(2274.5, 37.17) * mm, v(2271.07, 34.48) * mm, v(2267.76, 31.41) * mm, v(2264.53, 28.1) * mm, v(2261.36, 24.63) * mm, v(2258.24, 21.16) * mm, v(2255.17, 17.8) * mm, v(2251.1, 13.53) * mm, v(2247.1, 9.76) * mm, v(2243.18, 6.78) * mm, v(2240.28, 5.01) * mm, v(2237.45, 3.76) * mm, v(2235.62, 3.28) * mm, v(2234.7, 3.14) * mm]});
            skFitSpline(sketch, "E87.12", {"points": [v(2336.48, 3.16) * mm, v(2337.66, 3.28) * mm, v(2339.87, 3.72) * mm, v(2342.92, 4.91) * mm, v(2345.82, 6.62) * mm, v(2348.61, 8.8) * mm, v(2351.36, 11.42) * mm, v(2354.1, 14.39) * mm, v(2356.88, 17.64) * mm, v(2359.75, 21.08) * mm, v(2362.76, 24.62) * mm, v(2365.9, 28.12) * mm, v(2369.14, 31.47) * mm, v(2372.5, 34.55) * mm, v(2376, 37.23) * mm, v(2379.03, 39.04) * mm, v(2381.57, 40.15) * mm, v(2383.53, 40.78) * mm, v(2385.2, 41.11) * mm, v(2386.57, 41.25) * mm, v(2387.6, 41.29) * mm, v(2388.64, 41.25) * mm, v(2390, 41.1) * mm, v(2391.68, 40.75) * mm, v(2393.62, 40.11) * mm, v(2396.12, 38.99) * mm, v(2399.1, 37.17) * mm, v(2402.53, 34.48) * mm, v(2405.84, 31.41) * mm, v(2409.07, 28.1) * mm, v(2412.24, 24.63) * mm, v(2415.36, 21.16) * mm, v(2418.43, 17.8) * mm, v(2422.5, 13.53) * mm, v(2426.5, 9.76) * mm, v(2430.42, 6.78) * mm, v(2433.32, 5.01) * mm, v(2436.15, 3.76) * mm, v(2437.98, 3.28) * mm, v(2438.9, 3.14) * mm]});
            skFitSpline(sketch, "E87.13", {"points": [v(2540.32, 3.16) * mm, v(2539.14, 3.28) * mm, v(2536.93, 3.72) * mm, v(2533.88, 4.91) * mm, v(2530.98, 6.62) * mm, v(2528.19, 8.8) * mm, v(2525.44, 11.42) * mm, v(2522.7, 14.39) * mm, v(2519.92, 17.64) * mm, v(2517.05, 21.08) * mm, v(2514.04, 24.62) * mm, v(2510.9, 28.12) * mm, v(2507.66, 31.47) * mm, v(2504.3, 34.55) * mm, v(2500.8, 37.23) * mm, v(2497.77, 39.04) * mm, v(2495.23, 40.15) * mm, v(2493.27, 40.78) * mm, v(2491.6, 41.11) * mm, v(2490.23, 41.25) * mm, v(2489.2, 41.29) * mm, v(2488.16, 41.25) * mm, v(2486.8, 41.1) * mm, v(2485.12, 40.75) * mm, v(2483.18, 40.11) * mm, v(2480.68, 38.99) * mm, v(2477.7, 37.17) * mm, v(2474.27, 34.48) * mm, v(2470.96, 31.41) * mm, v(2467.73, 28.1) * mm, v(2464.56, 24.63) * mm, v(2461.44, 21.16) * mm, v(2458.37, 17.8) * mm, v(2454.3, 13.53) * mm, v(2450.3, 9.76) * mm, v(2446.38, 6.78) * mm, v(2443.48, 5.01) * mm, v(2440.65, 3.76) * mm, v(2438.82, 3.28) * mm, v(2437.9, 3.14) * mm]});
            skFitSpline(sketch, "E87.14", {"points": [v(2539.68, 3.16) * mm, v(2540.86, 3.28) * mm, v(2543.07, 3.72) * mm, v(2546.12, 4.91) * mm, v(2549.02, 6.62) * mm, v(2551.81, 8.8) * mm, v(2554.56, 11.42) * mm, v(2557.3, 14.39) * mm, v(2560.08, 17.64) * mm, v(2562.95, 21.08) * mm, v(2565.96, 24.62) * mm, v(2569.1, 28.12) * mm, v(2572.34, 31.47) * mm, v(2575.7, 34.55) * mm, v(2579.2, 37.23) * mm, v(2582.23, 39.04) * mm, v(2584.77, 40.15) * mm, v(2586.73, 40.78) * mm, v(2588.4, 41.11) * mm, v(2589.77, 41.25) * mm, v(2590.8, 41.29) * mm, v(2591.84, 41.25) * mm, v(2593.2, 41.1) * mm, v(2594.88, 40.75) * mm, v(2596.82, 40.11) * mm, v(2599.32, 38.99) * mm, v(2602.3, 37.17) * mm, v(2605.73, 34.48) * mm, v(2609.04, 31.41) * mm, v(2612.27, 28.1) * mm, v(2615.44, 24.63) * mm, v(2618.56, 21.16) * mm, v(2621.63, 17.8) * mm, v(2625.7, 13.53) * mm, v(2629.7, 9.76) * mm, v(2633.62, 6.78) * mm, v(2636.52, 5.01) * mm, v(2639.35, 3.76) * mm, v(2641.18, 3.28) * mm, v(2642.1, 3.14) * mm]});
            skFitSpline(sketch, "E87.15", {"points": [v(2743.52, 3.16) * mm, v(2742.34, 3.28) * mm, v(2740.13, 3.72) * mm, v(2737.08, 4.91) * mm, v(2734.18, 6.62) * mm, v(2731.39, 8.8) * mm, v(2728.64, 11.42) * mm, v(2725.9, 14.39) * mm, v(2723.12, 17.64) * mm, v(2720.25, 21.08) * mm, v(2717.24, 24.62) * mm, v(2714.1, 28.12) * mm, v(2710.86, 31.47) * mm, v(2707.5, 34.55) * mm, v(2704, 37.23) * mm, v(2700.97, 39.04) * mm, v(2698.43, 40.15) * mm, v(2696.47, 40.78) * mm, v(2694.8, 41.11) * mm, v(2693.43, 41.25) * mm, v(2692.4, 41.29) * mm, v(2691.36, 41.25) * mm, v(2690, 41.1) * mm, v(2688.32, 40.75) * mm, v(2686.38, 40.11) * mm, v(2683.88, 38.99) * mm, v(2680.9, 37.17) * mm, v(2677.47, 34.48) * mm, v(2674.16, 31.41) * mm, v(2670.93, 28.1) * mm, v(2667.76, 24.63) * mm, v(2664.64, 21.16) * mm, v(2661.57, 17.8) * mm, v(2657.5, 13.53) * mm, v(2653.5, 9.76) * mm, v(2649.58, 6.78) * mm, v(2646.68, 5.01) * mm, v(2643.85, 3.76) * mm, v(2642.02, 3.28) * mm, v(2641.1, 3.14) * mm]});
            skFitSpline(sketch, "E87.16", {"points": [v(3149.92, 3.16) * mm, v(3148.74, 3.28) * mm, v(3146.53, 3.72) * mm, v(3143.48, 4.91) * mm, v(3140.58, 6.62) * mm, v(3137.79, 8.8) * mm, v(3135.04, 11.42) * mm, v(3132.3, 14.39) * mm, v(3129.52, 17.64) * mm, v(3126.65, 21.08) * mm, v(3123.64, 24.62) * mm, v(3120.5, 28.12) * mm, v(3117.26, 31.47) * mm, v(3113.9, 34.55) * mm, v(3110.4, 37.23) * mm, v(3107.37, 39.04) * mm, v(3104.83, 40.15) * mm, v(3102.87, 40.78) * mm, v(3101.2, 41.11) * mm, v(3099.83, 41.25) * mm, v(3098.8, 41.29) * mm, v(3097.76, 41.25) * mm, v(3096.4, 41.1) * mm, v(3094.72, 40.75) * mm, v(3092.78, 40.11) * mm, v(3090.28, 38.99) * mm, v(3087.3, 37.17) * mm, v(3083.87, 34.48) * mm, v(3080.56, 31.41) * mm, v(3077.33, 28.1) * mm, v(3074.16, 24.63) * mm, v(3071.04, 21.16) * mm, v(3067.97, 17.8) * mm, v(3063.9, 13.53) * mm, v(3059.9, 9.76) * mm, v(3055.98, 6.78) * mm, v(3053.08, 5.01) * mm, v(3050.25, 3.76) * mm, v(3048.42, 3.28) * mm, v(3047.5, 3.14) * mm]});
            skFitSpline(sketch, "E87.17", {"points": [v(2946.08, 3.16) * mm, v(2947.26, 3.28) * mm, v(2949.47, 3.72) * mm, v(2952.52, 4.91) * mm, v(2955.42, 6.62) * mm, v(2958.21, 8.8) * mm, v(2960.96, 11.42) * mm, v(2963.7, 14.39) * mm, v(2966.48, 17.64) * mm, v(2969.35, 21.08) * mm, v(2972.36, 24.62) * mm, v(2975.5, 28.12) * mm, v(2978.74, 31.47) * mm, v(2982.1, 34.55) * mm, v(2985.6, 37.23) * mm, v(2988.63, 39.04) * mm, v(2991.17, 40.15) * mm, v(2993.13, 40.78) * mm, v(2994.8, 41.11) * mm, v(2996.17, 41.25) * mm, v(2997.2, 41.29) * mm, v(2998.24, 41.25) * mm, v(2999.6, 41.1) * mm, v(3001.28, 40.75) * mm, v(3003.22, 40.11) * mm, v(3005.72, 38.99) * mm, v(3008.7, 37.17) * mm, v(3012.13, 34.48) * mm, v(3015.44, 31.41) * mm, v(3018.67, 28.1) * mm, v(3021.84, 24.63) * mm, v(3024.96, 21.16) * mm, v(3028.03, 17.8) * mm, v(3032.1, 13.53) * mm, v(3036.1, 9.76) * mm, v(3040.02, 6.78) * mm, v(3042.92, 5.01) * mm, v(3045.75, 3.76) * mm, v(3047.58, 3.28) * mm, v(3048.5, 3.14) * mm]});
            skFitSpline(sketch, "E87.18", {"points": [v(2946.72, 3.16) * mm, v(2945.54, 3.28) * mm, v(2943.33, 3.72) * mm, v(2940.28, 4.91) * mm, v(2937.38, 6.62) * mm, v(2934.59, 8.8) * mm, v(2931.84, 11.42) * mm, v(2929.1, 14.39) * mm, v(2926.32, 17.64) * mm, v(2923.45, 21.08) * mm, v(2920.44, 24.62) * mm, v(2917.3, 28.12) * mm, v(2914.06, 31.47) * mm, v(2910.7, 34.55) * mm, v(2907.2, 37.23) * mm, v(2904.17, 39.04) * mm, v(2901.63, 40.15) * mm, v(2899.67, 40.78) * mm, v(2898, 41.11) * mm, v(2896.63, 41.25) * mm, v(2895.6, 41.29) * mm, v(2894.56, 41.25) * mm, v(2893.2, 41.1) * mm, v(2891.52, 40.75) * mm, v(2889.58, 40.11) * mm, v(2887.08, 38.99) * mm, v(2884.1, 37.17) * mm, v(2880.67, 34.48) * mm, v(2877.36, 31.41) * mm, v(2874.13, 28.1) * mm, v(2870.96, 24.63) * mm, v(2867.84, 21.16) * mm, v(2864.77, 17.8) * mm, v(2860.7, 13.53) * mm, v(2856.7, 9.76) * mm, v(2852.78, 6.78) * mm, v(2849.88, 5.01) * mm, v(2847.05, 3.76) * mm, v(2845.22, 3.28) * mm, v(2844.3, 3.14) * mm]});
            skFitSpline(sketch, "E87.19", {"points": [v(2742.88, 3.16) * mm, v(2744.06, 3.28) * mm, v(2746.27, 3.72) * mm, v(2749.32, 4.91) * mm, v(2752.22, 6.62) * mm, v(2755.01, 8.8) * mm, v(2757.76, 11.42) * mm, v(2760.5, 14.39) * mm, v(2763.28, 17.64) * mm, v(2766.15, 21.08) * mm, v(2769.16, 24.62) * mm, v(2772.3, 28.12) * mm, v(2775.54, 31.47) * mm, v(2778.9, 34.55) * mm, v(2782.4, 37.23) * mm, v(2785.43, 39.04) * mm, v(2787.97, 40.15) * mm, v(2789.93, 40.78) * mm, v(2791.6, 41.11) * mm, v(2792.97, 41.25) * mm, v(2794, 41.29) * mm, v(2795.04, 41.25) * mm, v(2796.4, 41.1) * mm, v(2798.08, 40.75) * mm, v(2800.02, 40.11) * mm, v(2802.52, 38.99) * mm, v(2805.5, 37.17) * mm, v(2808.93, 34.48) * mm, v(2812.24, 31.41) * mm, v(2815.47, 28.1) * mm, v(2818.64, 24.63) * mm, v(2821.76, 21.16) * mm, v(2824.83, 17.8) * mm, v(2828.9, 13.53) * mm, v(2832.9, 9.76) * mm, v(2836.82, 6.78) * mm, v(2839.72, 5.01) * mm, v(2842.55, 3.76) * mm, v(2844.38, 3.28) * mm, v(2845.3, 3.14) * mm]});
            skFitSpline(sketch, "E87.20", {"points": [v(2133.92, 3.16) * mm, v(2132.74, 3.28) * mm, v(2130.53, 3.72) * mm, v(2127.48, 4.91) * mm, v(2124.58, 6.62) * mm, v(2121.79, 8.8) * mm, v(2119.04, 11.42) * mm, v(2116.3, 14.39) * mm, v(2113.52, 17.64) * mm, v(2110.65, 21.08) * mm, v(2107.64, 24.62) * mm, v(2104.5, 28.12) * mm, v(2101.26, 31.47) * mm, v(2097.9, 34.55) * mm, v(2094.4, 37.23) * mm, v(2091.37, 39.04) * mm, v(2088.83, 40.15) * mm, v(2086.87, 40.78) * mm, v(2085.2, 41.11) * mm, v(2083.83, 41.25) * mm, v(2082.8, 41.29) * mm, v(2081.76, 41.25) * mm, v(2080.4, 41.1) * mm, v(2078.72, 40.75) * mm, v(2076.78, 40.11) * mm, v(2074.28, 38.99) * mm, v(2071.3, 37.17) * mm, v(2067.87, 34.48) * mm, v(2064.56, 31.41) * mm, v(2061.33, 28.1) * mm, v(2058.16, 24.63) * mm, v(2055.04, 21.16) * mm, v(2051.97, 17.8) * mm, v(2047.9, 13.53) * mm, v(2043.9, 9.76) * mm, v(2039.98, 6.78) * mm, v(2037.08, 5.01) * mm, v(2034.25, 3.76) * mm, v(2032.42, 3.28) * mm, v(2031.5, 3.14) * mm]});
            skFitSpline(sketch, "E87.21", {"points": [v(1930.08, 3.16) * mm, v(1931.26, 3.28) * mm, v(1933.47, 3.72) * mm, v(1936.52, 4.91) * mm, v(1939.42, 6.62) * mm, v(1942.21, 8.8) * mm, v(1944.96, 11.42) * mm, v(1947.7, 14.39) * mm, v(1950.48, 17.64) * mm, v(1953.35, 21.08) * mm, v(1956.36, 24.62) * mm, v(1959.5, 28.12) * mm, v(1962.74, 31.47) * mm, v(1966.1, 34.55) * mm, v(1969.6, 37.23) * mm, v(1972.63, 39.04) * mm, v(1975.17, 40.15) * mm, v(1977.13, 40.78) * mm, v(1978.8, 41.11) * mm, v(1980.17, 41.25) * mm, v(1981.2, 41.29) * mm, v(1982.24, 41.25) * mm, v(1983.6, 41.1) * mm, v(1985.28, 40.75) * mm, v(1987.22, 40.11) * mm, v(1989.72, 38.99) * mm, v(1992.7, 37.17) * mm, v(1996.13, 34.48) * mm, v(1999.44, 31.41) * mm, v(2002.67, 28.1) * mm, v(2005.84, 24.63) * mm, v(2008.96, 21.16) * mm, v(2012.03, 17.8) * mm, v(2016.1, 13.53) * mm, v(2020.1, 9.76) * mm, v(2024.02, 6.78) * mm, v(2026.92, 5.01) * mm, v(2029.75, 3.76) * mm, v(2031.58, 3.28) * mm, v(2032.5, 3.14) * mm]});
            skFitSpline(sketch, "E87.22", {"points": [v(1930.72, 3.16) * mm, v(1929.54, 3.28) * mm, v(1927.33, 3.72) * mm, v(1924.28, 4.91) * mm, v(1921.38, 6.62) * mm, v(1918.59, 8.8) * mm, v(1915.84, 11.42) * mm, v(1913.1, 14.39) * mm, v(1910.32, 17.64) * mm, v(1907.45, 21.08) * mm, v(1904.44, 24.62) * mm, v(1901.3, 28.12) * mm, v(1898.06, 31.47) * mm, v(1894.7, 34.55) * mm, v(1891.2, 37.23) * mm, v(1888.17, 39.04) * mm, v(1885.63, 40.15) * mm, v(1883.67, 40.78) * mm, v(1882, 41.11) * mm, v(1880.63, 41.25) * mm, v(1879.6, 41.29) * mm, v(1878.56, 41.25) * mm, v(1877.2, 41.1) * mm, v(1875.52, 40.75) * mm, v(1873.58, 40.11) * mm, v(1871.08, 38.99) * mm, v(1868.1, 37.17) * mm, v(1864.67, 34.48) * mm, v(1861.36, 31.41) * mm, v(1858.13, 28.1) * mm, v(1854.96, 24.63) * mm, v(1851.84, 21.16) * mm, v(1848.77, 17.8) * mm, v(1844.7, 13.53) * mm, v(1840.7, 9.76) * mm, v(1836.78, 6.78) * mm, v(1833.88, 5.01) * mm, v(1831.05, 3.76) * mm, v(1829.22, 3.28) * mm, v(1828.3, 3.14) * mm]});
            skFitSpline(sketch, "E87.23", {"points": [v(1726.88, 3.16) * mm, v(1728.06, 3.28) * mm, v(1730.27, 3.72) * mm, v(1733.32, 4.91) * mm, v(1736.22, 6.62) * mm, v(1739.01, 8.8) * mm, v(1741.76, 11.42) * mm, v(1744.5, 14.39) * mm, v(1747.28, 17.64) * mm, v(1750.15, 21.08) * mm, v(1753.16, 24.62) * mm, v(1756.3, 28.12) * mm, v(1759.54, 31.47) * mm, v(1762.9, 34.55) * mm, v(1766.4, 37.23) * mm, v(1769.43, 39.04) * mm, v(1771.97, 40.15) * mm, v(1773.93, 40.78) * mm, v(1775.6, 41.11) * mm, v(1776.97, 41.25) * mm, v(1778, 41.29) * mm, v(1779.04, 41.25) * mm, v(1780.4, 41.1) * mm, v(1782.08, 40.75) * mm, v(1784.02, 40.11) * mm, v(1786.52, 38.99) * mm, v(1789.5, 37.17) * mm, v(1792.93, 34.48) * mm, v(1796.24, 31.41) * mm, v(1799.47, 28.1) * mm, v(1802.64, 24.63) * mm, v(1805.76, 21.16) * mm, v(1808.83, 17.8) * mm, v(1812.9, 13.53) * mm, v(1816.9, 9.76) * mm, v(1820.82, 6.78) * mm, v(1823.72, 5.01) * mm, v(1826.55, 3.76) * mm, v(1828.38, 3.28) * mm, v(1829.3, 3.14) * mm]});
            skFitSpline(sketch, "E87.24", {"points": [v(1727.52, 3.16) * mm, v(1726.34, 3.28) * mm, v(1724.13, 3.72) * mm, v(1721.08, 4.91) * mm, v(1718.18, 6.62) * mm, v(1715.39, 8.8) * mm, v(1712.64, 11.42) * mm, v(1709.9, 14.39) * mm, v(1707.12, 17.64) * mm, v(1704.25, 21.08) * mm, v(1701.24, 24.62) * mm, v(1698.1, 28.12) * mm, v(1694.86, 31.47) * mm, v(1691.5, 34.55) * mm, v(1688, 37.23) * mm, v(1684.97, 39.04) * mm, v(1682.43, 40.15) * mm, v(1680.47, 40.78) * mm, v(1678.8, 41.11) * mm, v(1677.43, 41.25) * mm, v(1676.4, 41.29) * mm, v(1675.36, 41.25) * mm, v(1674, 41.1) * mm, v(1672.32, 40.75) * mm, v(1670.38, 40.11) * mm, v(1667.88, 38.99) * mm, v(1664.9, 37.17) * mm, v(1661.47, 34.48) * mm, v(1658.16, 31.41) * mm, v(1654.93, 28.1) * mm, v(1651.76, 24.63) * mm, v(1648.64, 21.16) * mm, v(1645.57, 17.8) * mm, v(1641.5, 13.53) * mm, v(1637.5, 9.76) * mm, v(1633.58, 6.78) * mm, v(1630.68, 5.01) * mm, v(1627.85, 3.76) * mm, v(1626.02, 3.28) * mm, v(1625.1, 3.14) * mm]});
            skFitSpline(sketch, "E87.25", {"points": [v(1523.68, 3.16) * mm, v(1524.86, 3.28) * mm, v(1527.07, 3.72) * mm, v(1530.12, 4.91) * mm, v(1533.02, 6.62) * mm, v(1535.81, 8.8) * mm, v(1538.56, 11.42) * mm, v(1541.3, 14.39) * mm, v(1544.08, 17.64) * mm, v(1546.95, 21.08) * mm, v(1549.96, 24.62) * mm, v(1553.1, 28.12) * mm, v(1556.34, 31.47) * mm, v(1559.7, 34.55) * mm, v(1563.2, 37.23) * mm, v(1566.23, 39.04) * mm, v(1568.77, 40.15) * mm, v(1570.73, 40.78) * mm, v(1572.4, 41.11) * mm, v(1573.77, 41.25) * mm, v(1574.8, 41.29) * mm, v(1575.84, 41.25) * mm, v(1577.2, 41.1) * mm, v(1578.88, 40.75) * mm, v(1580.82, 40.11) * mm, v(1583.32, 38.99) * mm, v(1586.3, 37.17) * mm, v(1589.73, 34.48) * mm, v(1593.04, 31.41) * mm, v(1596.27, 28.1) * mm, v(1599.44, 24.63) * mm, v(1602.56, 21.16) * mm, v(1605.63, 17.8) * mm, v(1609.7, 13.53) * mm, v(1613.7, 9.76) * mm, v(1617.62, 6.78) * mm, v(1620.52, 5.01) * mm, v(1623.35, 3.76) * mm, v(1625.18, 3.28) * mm, v(1626.1, 3.14) * mm]});
            skFitSpline(sketch, "E87.26", {"points": [v(1524.32, 3.16) * mm, v(1523.14, 3.28) * mm, v(1520.93, 3.72) * mm, v(1517.88, 4.91) * mm, v(1514.98, 6.62) * mm, v(1512.19, 8.8) * mm, v(1509.44, 11.42) * mm, v(1506.7, 14.39) * mm, v(1503.92, 17.64) * mm, v(1501.05, 21.08) * mm, v(1498.04, 24.62) * mm, v(1494.9, 28.12) * mm, v(1491.66, 31.47) * mm, v(1488.3, 34.55) * mm, v(1484.8, 37.23) * mm, v(1481.77, 39.04) * mm, v(1479.23, 40.15) * mm, v(1477.27, 40.78) * mm, v(1475.6, 41.11) * mm, v(1474.23, 41.25) * mm, v(1473.2, 41.29) * mm, v(1472.16, 41.25) * mm, v(1470.8, 41.1) * mm, v(1469.12, 40.75) * mm, v(1467.18, 40.11) * mm, v(1464.68, 38.99) * mm, v(1461.7, 37.17) * mm, v(1458.27, 34.48) * mm, v(1454.96, 31.41) * mm, v(1451.73, 28.1) * mm, v(1448.56, 24.63) * mm, v(1445.44, 21.16) * mm, v(1442.37, 17.8) * mm, v(1438.3, 13.53) * mm, v(1434.3, 9.76) * mm, v(1430.38, 6.78) * mm, v(1427.48, 5.01) * mm, v(1424.65, 3.76) * mm, v(1422.82, 3.28) * mm, v(1421.9, 3.14) * mm]});
            skFitSpline(sketch, "E87.27", {"points": [v(1320.48, 3.16) * mm, v(1321.66, 3.28) * mm, v(1323.87, 3.72) * mm, v(1326.92, 4.91) * mm, v(1329.82, 6.62) * mm, v(1332.61, 8.8) * mm, v(1335.36, 11.42) * mm, v(1338.1, 14.39) * mm, v(1340.88, 17.64) * mm, v(1343.75, 21.08) * mm, v(1346.76, 24.62) * mm, v(1349.9, 28.12) * mm, v(1353.14, 31.47) * mm, v(1356.5, 34.55) * mm, v(1360, 37.23) * mm, v(1363.03, 39.04) * mm, v(1365.57, 40.15) * mm, v(1367.53, 40.78) * mm, v(1369.2, 41.11) * mm, v(1370.57, 41.25) * mm, v(1371.6, 41.29) * mm, v(1372.64, 41.25) * mm, v(1374, 41.1) * mm, v(1375.68, 40.75) * mm, v(1377.62, 40.11) * mm, v(1380.12, 38.99) * mm, v(1383.1, 37.17) * mm, v(1386.53, 34.48) * mm, v(1389.84, 31.41) * mm, v(1393.07, 28.1) * mm, v(1396.24, 24.63) * mm, v(1399.36, 21.16) * mm, v(1402.43, 17.8) * mm, v(1406.5, 13.53) * mm, v(1410.5, 9.76) * mm, v(1414.42, 6.78) * mm, v(1417.32, 5.01) * mm, v(1420.15, 3.76) * mm, v(1421.98, 3.28) * mm, v(1422.9, 3.14) * mm]});
            skFitSpline(sketch, "E87.28", {"points": [v(1321.12, 3.16) * mm, v(1319.94, 3.28) * mm, v(1317.73, 3.72) * mm, v(1314.68, 4.91) * mm, v(1311.78, 6.62) * mm, v(1308.99, 8.8) * mm, v(1306.24, 11.42) * mm, v(1303.5, 14.39) * mm, v(1300.72, 17.64) * mm, v(1297.85, 21.08) * mm, v(1294.84, 24.62) * mm, v(1291.7, 28.12) * mm, v(1288.46, 31.47) * mm, v(1285.1, 34.55) * mm, v(1281.6, 37.23) * mm, v(1278.57, 39.04) * mm, v(1276.03, 40.15) * mm, v(1274.07, 40.78) * mm, v(1272.4, 41.11) * mm, v(1271.03, 41.25) * mm, v(1270, 41.29) * mm, v(1268.96, 41.25) * mm, v(1267.6, 41.1) * mm, v(1265.92, 40.75) * mm, v(1263.98, 40.11) * mm, v(1261.48, 38.99) * mm, v(1258.5, 37.17) * mm, v(1255.07, 34.48) * mm, v(1251.76, 31.41) * mm, v(1248.53, 28.1) * mm, v(1245.36, 24.63) * mm, v(1242.24, 21.16) * mm, v(1239.17, 17.8) * mm, v(1235.1, 13.53) * mm, v(1231.1, 9.76) * mm, v(1227.18, 6.78) * mm, v(1224.28, 5.01) * mm, v(1221.45, 3.76) * mm, v(1219.62, 3.28) * mm, v(1218.7, 3.14) * mm]});
            skFitSpline(sketch, "E87.29", {"points": [v(1117.28, 3.16) * mm, v(1118.46, 3.28) * mm, v(1120.67, 3.72) * mm, v(1123.72, 4.91) * mm, v(1126.62, 6.62) * mm, v(1129.41, 8.8) * mm, v(1132.16, 11.42) * mm, v(1134.9, 14.39) * mm, v(1137.68, 17.64) * mm, v(1140.55, 21.08) * mm, v(1143.56, 24.62) * mm, v(1146.7, 28.12) * mm, v(1149.94, 31.47) * mm, v(1153.3, 34.55) * mm, v(1156.8, 37.23) * mm, v(1159.83, 39.04) * mm, v(1162.37, 40.15) * mm, v(1164.33, 40.78) * mm, v(1166, 41.11) * mm, v(1167.37, 41.25) * mm, v(1168.4, 41.29) * mm, v(1169.44, 41.25) * mm, v(1170.8, 41.1) * mm, v(1172.48, 40.75) * mm, v(1174.42, 40.11) * mm, v(1176.92, 38.99) * mm, v(1179.9, 37.17) * mm, v(1183.33, 34.48) * mm, v(1186.64, 31.41) * mm, v(1189.87, 28.1) * mm, v(1193.04, 24.63) * mm, v(1196.16, 21.16) * mm, v(1199.23, 17.8) * mm, v(1203.3, 13.53) * mm, v(1207.3, 9.76) * mm, v(1211.22, 6.78) * mm, v(1214.12, 5.01) * mm, v(1216.95, 3.76) * mm, v(1218.78, 3.28) * mm, v(1219.7, 3.14) * mm]});
            skFitSpline(sketch, "E87.30", {"points": [v(1117.92, 3.16) * mm, v(1116.74, 3.28) * mm, v(1114.53, 3.72) * mm, v(1111.48, 4.91) * mm, v(1108.58, 6.62) * mm, v(1105.79, 8.8) * mm, v(1103.04, 11.42) * mm, v(1100.3, 14.39) * mm, v(1097.52, 17.64) * mm, v(1094.65, 21.08) * mm, v(1091.64, 24.62) * mm, v(1088.5, 28.12) * mm, v(1085.26, 31.47) * mm, v(1081.9, 34.55) * mm, v(1078.4, 37.23) * mm, v(1075.37, 39.04) * mm, v(1072.83, 40.15) * mm, v(1070.87, 40.78) * mm, v(1069.2, 41.11) * mm, v(1067.83, 41.25) * mm, v(1066.8, 41.29) * mm, v(1065.76, 41.25) * mm, v(1064.4, 41.1) * mm, v(1062.72, 40.75) * mm, v(1060.78, 40.11) * mm, v(1058.28, 38.99) * mm, v(1055.3, 37.17) * mm, v(1051.87, 34.48) * mm, v(1048.56, 31.41) * mm, v(1045.33, 28.1) * mm, v(1042.16, 24.63) * mm, v(1039.04, 21.16) * mm, v(1035.97, 17.8) * mm, v(1031.9, 13.53) * mm, v(1027.9, 9.76) * mm, v(1023.98, 6.78) * mm, v(1021.08, 5.01) * mm, v(1018.25, 3.76) * mm, v(1016.42, 3.28) * mm, v(1015.5, 3.14) * mm]});
            skFitSpline(sketch, "E87.31", {"points": [v(914.08, 3.16) * mm, v(915.26, 3.28) * mm, v(917.47, 3.72) * mm, v(920.52, 4.91) * mm, v(923.42, 6.62) * mm, v(926.21, 8.8) * mm, v(928.96, 11.42) * mm, v(931.7, 14.39) * mm, v(934.48, 17.64) * mm, v(937.35, 21.08) * mm, v(940.36, 24.62) * mm, v(943.5, 28.12) * mm, v(946.74, 31.47) * mm, v(950.1, 34.55) * mm, v(953.6, 37.23) * mm, v(956.63, 39.04) * mm, v(959.17, 40.15) * mm, v(961.13, 40.78) * mm, v(962.8, 41.11) * mm, v(964.17, 41.25) * mm, v(965.2, 41.29) * mm, v(966.24, 41.25) * mm, v(967.6, 41.1) * mm, v(969.28, 40.75) * mm, v(971.22, 40.11) * mm, v(973.72, 38.99) * mm, v(976.7, 37.17) * mm, v(980.13, 34.48) * mm, v(983.44, 31.41) * mm, v(986.67, 28.1) * mm, v(989.84, 24.63) * mm, v(992.96, 21.16) * mm, v(996.03, 17.8) * mm, v(1000.1, 13.53) * mm, v(1004.1, 9.76) * mm, v(1008.02, 6.78) * mm, v(1010.92, 5.01) * mm, v(1013.75, 3.76) * mm, v(1015.58, 3.28) * mm, v(1016.5, 3.14) * mm]});
            skLineSegment(sketch, "E88", {"start": v(-101.92, 3.16) * mm, "end": v(-101.6, 0) * mm});
            skLineSegment(sketch, "E89", {"start": v(3149.6, 0) * mm, "end": v(3149.92, 3.16) * mm});
            skLineSegment(sketch, "E90", {"start": v(3048, 0) * mm, "end": v(3048, 3.22) * mm});
            skLineSegment(sketch, "E91", {"start": v(2946.4, 0) * mm, "end": v(2946.4, 3.2) * mm});
            skLineSegment(sketch, "E92", {"start": v(2336.8, 0) * mm, "end": v(2336.8, 3.2) * mm});
            skSolve(sketch);
        }
        {
            var Q0;
            Q0=makeQuery(id+"F0.imprint","IMPRINT",FACE,{"disambiguationData":[TD([[makeQuery(id+"F0.imprint","IMPRINT",EDGE,{"derivedFrom":sQuery(id+"F0.wireOp",EDGE,"E0")}),1.0]])]});
            extrude(context, id + "F1", {"entities" : qUnion([Q0]), "depth" : 2006.6 * mm});
        }
    });
